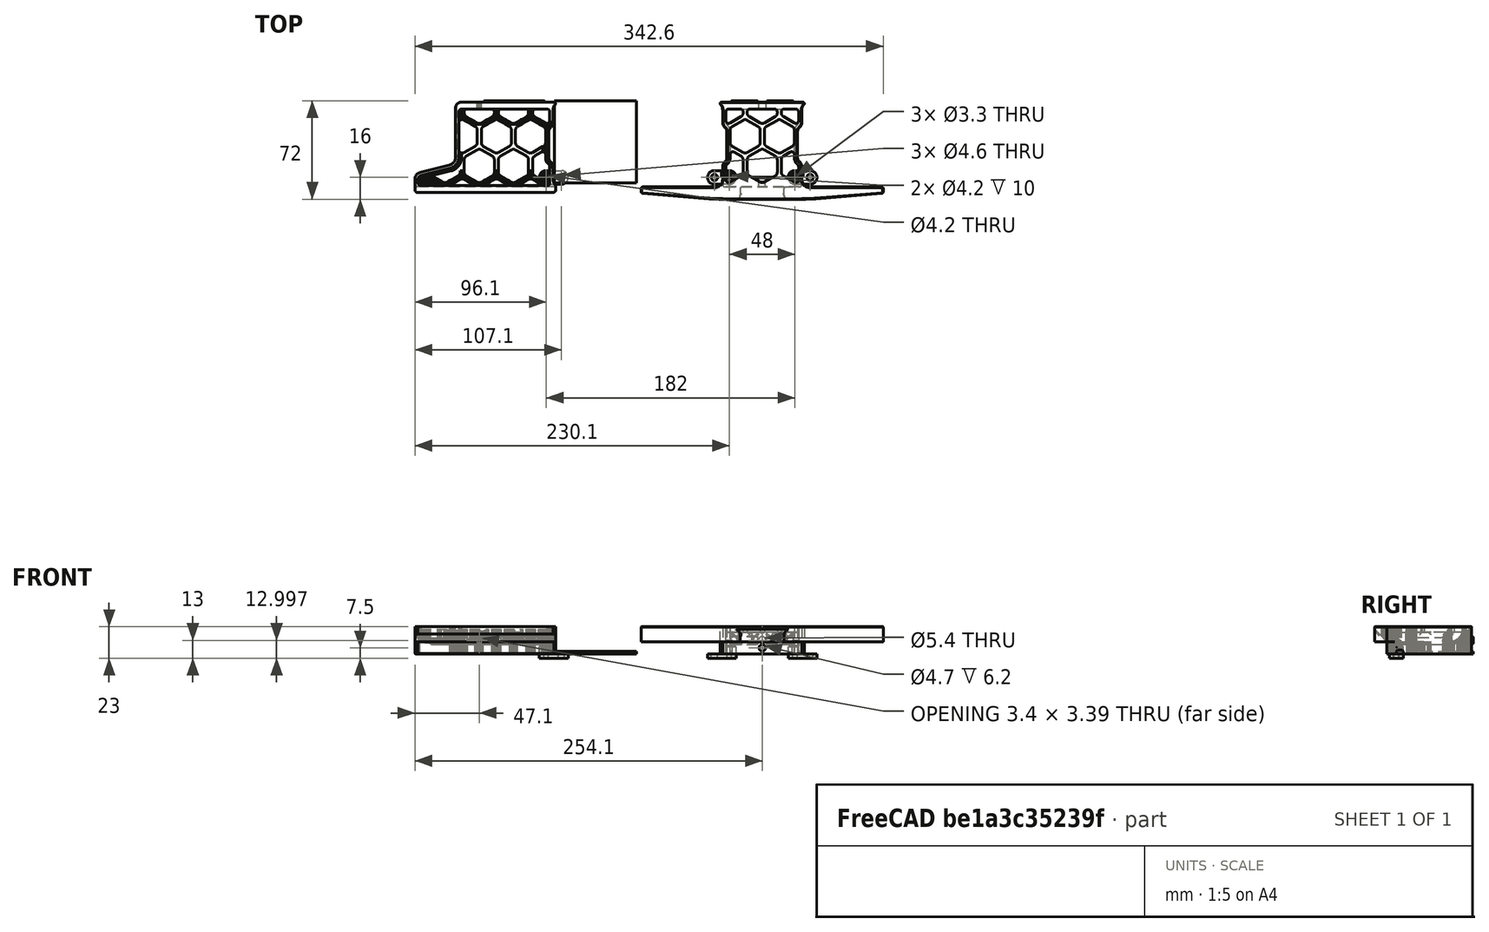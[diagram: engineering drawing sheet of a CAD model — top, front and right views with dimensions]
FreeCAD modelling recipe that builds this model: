
FCSTD DOCUMENT  (FreeCAD 0.18R16146 (Git))
Label: skirt-fan-connector
License: Other
LicenseURL: GPL3
objects: Part::Cylinder×8, Part::MultiFuse×6, Part::Feature×4, Part::Box×3, Part::Chamfer×3, Part::Cut×3, Part::Fillet×1
note: 28 computed .brp shape members not serialized (recipe doc carries the construction recipe); baked Part::Feature solids carry a one-line shape summary decoded from their .brp

FEATURE [Part::Cylinder] Cylinder
  Angle = 360
  AttacherType = Attacher::AttachEngine3D
  Height = 10
  Placement = pos=(-6,-55,-3) rot=(0,0,1;0rad)
  Radius = 1.65
FEATURE [Part::Cylinder] Cylinder001
  Angle = 360
  AttacherType = Attacher::AttachEngine3D
  Height = 10
  Placement = pos=(5,-55,-3) rot=(0,0,1;0rad)
  Radius = 2.3
FEATURE [Part::Box] Box  label="Cube"
  AttacherType = Attacher::AttachEngine3D
  Height = 2
  Length = 60
  Placement = pos=(0,-59,0) rot=(0,0,1;0rad)
  Width = 60
FEATURE [Part::Cylinder] Cylinder002
  Angle = 360
  AttacherType = Attacher::AttachEngine3D
  Height = 6
  Placement = pos=(-6,-55,0) rot=(0,0,1;0rad)
  Radius = 5
FEATURE [Part::Cylinder] Cylinder003
  Angle = 360
  AttacherType = Attacher::AttachEngine3D
  Height = 10
  Placement = pos=(-6,-55,0) rot=(0,0,1;0rad)
  Radius = 2.1
FEATURE [Part::Chamfer] Chamfer
  Base = -> Cylinder002
  Edges = 1 edges r=1: [Edge1]
FEATURE [Part::Box] Box001  label="Cube001"
  AttacherType = Attacher::AttachEngine3D
  Height = 3
  Length = 21
  Placement = pos=(-11,-60,-3) rot=(0,0,1;0rad)
  Width = 10
FEATURE [Part::Fillet] Fillet
  Base = -> Box001
  Edges = 4 edges r=4.99: [Edge1,Edge3,Edge5,Edge7]
FEATURE [Part::MultiFuse] Fusion001
  Shapes = -> [Cylinder,Cylinder001]
FEATURE [Part::Cut] Cut001
  Base = -> Fillet
  Tool = -> Fusion001
FEATURE [Part::Box] Box002  label="Cube002"
  AttacherType = Attacher::AttachEngine3D
  Height = 3
  Length = 0.8
  Placement = pos=(-0.9,-55,0) rot=(0,0,1;0rad)
  Width = 5
FEATURE [Part::Chamfer] Chamfer001
  Base = -> Box002
  Edges = 2 edges r=1: [Edge10,Edge12]
FEATURE [Part::MultiFuse] Fusion002  label="connector"
  Shapes = -> [Cut001,Chamfer001]
FEATURE [Part::Feature] Part__Feature1600  label="SOLID115"
  Placement = pos=(319,58.1,331.8) rot=(0.57735,-0.57735,-0.57735;4.18879rad)
  shape: bbox 177 x 72.31 x 20.01 mm, 232 faces (baked)
FEATURE [Part::Cylinder] Cylinder004
  Angle = 360
  AttacherType = Attacher::AttachEngine3D
  Height = 6
  Placement = pos=(128,-55,0) rot=(0,0,1;0rad)
  Radius = 5
FEATURE [Part::Cylinder] Cylinder005
  Angle = 360
  AttacherType = Attacher::AttachEngine3D
  Height = 10
  Placement = pos=(128,-55,0) rot=(0,0,1;0rad)
  Radius = 2.1
FEATURE [Part::Feature] Fusion002001  label="connector001"
  Placement = pos=(182,0,0) rot=(0,0,1;0rad)
  shape: bbox 21 x 10 x 6 mm, 18 faces (baked)
FEATURE [Part::Feature] Part__Mirroring001  label="connector (Mirror #1)001"
  Placement = pos=(122,0,0) rot=(0,0,1;0rad)
  shape: bbox 21 x 10 x 6 mm, 18 faces (baked)
FEATURE [Part::Cylinder] Cylinder006
  Angle = 360
  AttacherType = Attacher::AttachEngine3D
  Height = 10
  Placement = pos=(176,-55,0) rot=(0,0,1;0rad)
  Radius = 2.1
FEATURE [Part::Cylinder] Cylinder007
  Angle = 360
  AttacherType = Attacher::AttachEngine3D
  Height = 6
  Placement = pos=(176,-55,0) rot=(0,0,1;0rad)
  Radius = 5
FEATURE [Part::MultiFuse] Fusion002003
  Shapes = -> [Cylinder005,Cylinder006]
FEATURE [Part::MultiFuse] Fusion002002
  Shapes = -> [Cylinder004,Cylinder007]
FEATURE [Part::Chamfer] Chamfer002
  Base = -> Fusion002002
  Edges = 2 edges r=1: [Edge1,Edge4]
FEATURE [Part::MultiFuse] Fusion002004
  Shapes = -> [Part__Feature1600,Chamfer002]
FEATURE [Part::Cut] Cut002  label="mid-mounter"
  Base = -> Fusion002004
  Tool = -> Fusion002003
FEATURE [Part::Feature] side_skirt_a_300_x2001001_solid  label="side_skirt_a_300_x2002 (Solid)"
  Placement = pos=(-175.55,92.5,0) rot=(0,0,1;4.71239rad)
  shape: bbox 103.1 x 67 x 20 mm, 6829 faces (baked)
FEATURE [Part::MultiFuse] Fusion
  Shapes = -> [Chamfer,side_skirt_a_300_x2001001_solid]
FEATURE [Part::Cut] Cut
  Base = -> Fusion
  Tool = -> Cylinder003
